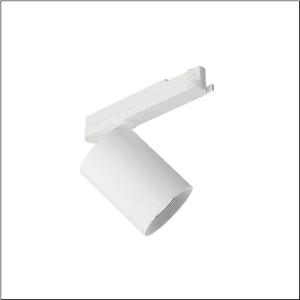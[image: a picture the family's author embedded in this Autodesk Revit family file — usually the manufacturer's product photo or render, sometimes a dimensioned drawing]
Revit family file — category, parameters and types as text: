
# Revit family: spot_21_51se12mba5b
name_source: partatom
category: Lighting Fixtures
units: mm (PartAtom-declared; Revit-internal decimal feet)

## family parameters
Cut with Voids When Loaded = No
Host = Face
Light Source = No
Part Type = Normal
Room Calculation Point = No
Round Connector Dimension = Use Diameter
Shared = No

## types (1)
- --- (1 x LED, 5240 lm, 41.7 W, 2700K)
    Apparent Load = 42 VA
    CIE Flux Codes = 95 98 99 100 100
    Color Rendering = 90
    Color Temperature = 2700K
    Default Elevation = 1800 mm
    Description = Spot 21, directional spotlight, light control with lens, of PMMA, LED rated luminous flux: 5.040lm, light colour: 927, control gear: ECG Multilumen, with 3-phase adapter, mains connection: 220..240V, AC, 50/60Hz, of aluminium, traffic white (RAL 9016), length: 213mm, diameter: 105mm, protection rating (complete): IP20, insulation class (complete): insulation class I (protective earthing), certification: CE, impact resistance: IK02, permissible ambient temperature for indoor applications: -20..+40°C, packaging unit: 1 piece
    Height = 175 mm
    Lamp = 1 x LED
    Lamp Light Flux = 5240 lm
    Lamp Power = 41.7 W
    Lamp count = 1
    Length = 105 mm
    Luminous efficacy = 126 lm/W
    Manufacturer = Siteco
    ModVariant = No
    Model = 51SE12MBA5B
    Mounting Place = Ceiling
    Mounting Type = Pendant
    Number of Poles = 1
    OnlyDefault = Yes
    Power Factor = 1
    Product Name = Spot 21
    Product group = directional spotlight
    ProductGroupID = 905
    Protection Class = Protection class I
    Protection Degree = IP 20
    RLX_Detail_Level = 1
    RLX_Emergency_Light_Flux = 0 lm
    RLX_Emergency_Type = 0
    RLX_Emergency_Type_DB = No
    RlxData = <blob elided: 17645 chars, md5=92f21c83>
    Socket = socket
    Standby Power = 0 W
    System Light Flux = 5240 lm
    System Power = 42 W
    Type Comments = factory setting: luminous flux: 100 % | (ON | ON | ON | ON) | 1050 mA
    Type Image = l_1003976.jpg
    URL = http://relux.com
    VarID = @adj_094001
    Voltage = 0 V
    Weight = 0.00 kg
    Width = 0 mm  [stored 0 ft]

note: [stored X ft] marks values corroborated as IEEE doubles in the binary element streams (Revit-internal decimal feet)

## geometry (parser evidence)
native form markers: Blend x4, Sweep x12
no freeform markers — native parametric forms only
